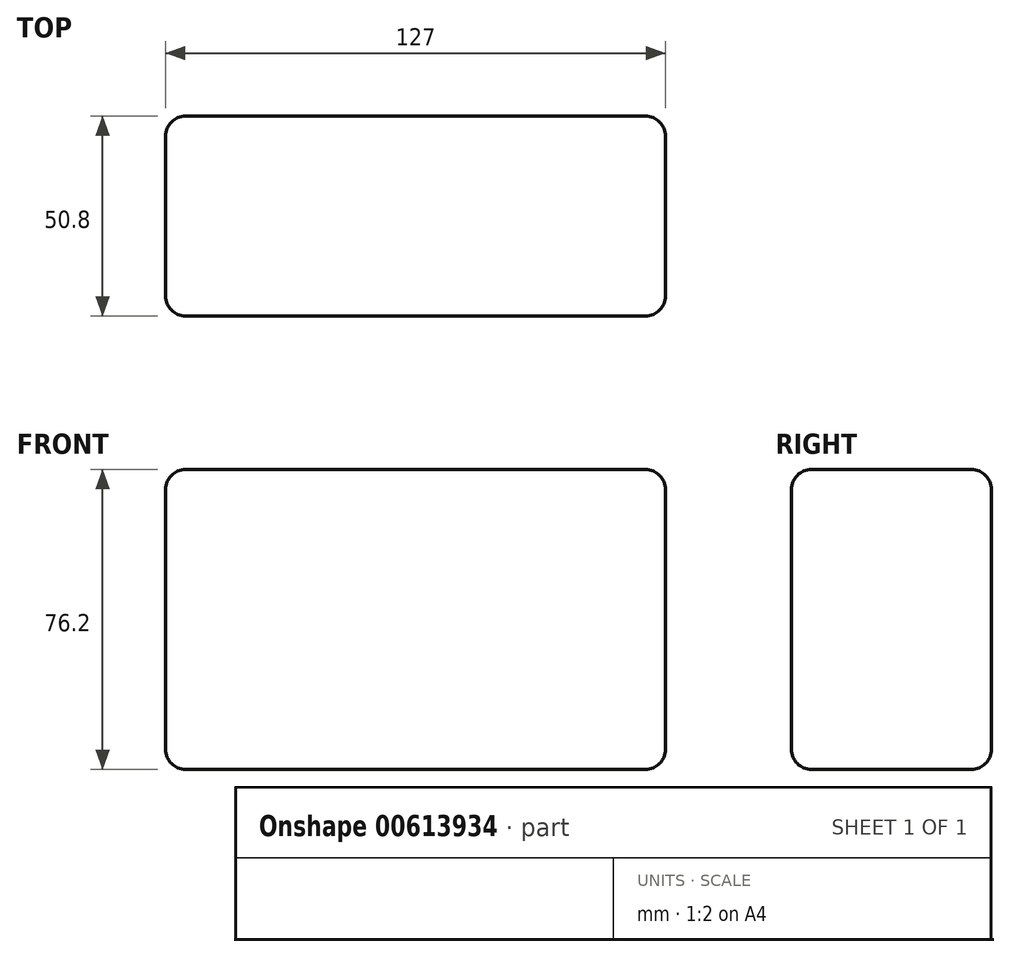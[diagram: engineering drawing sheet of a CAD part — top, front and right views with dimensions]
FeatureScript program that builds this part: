
annotation { "Feature Type Name" : "Feature", "Feature Type Description" : "" }
export const myFeature = defineFeature(function(context is Context, id is Id, definition is map)
    precondition{}
    {
        {
            var Q0;
            Q0=qCreatedBy(makeId("Top.planeOp"),FACE);
            var sketch = newSketch(context, id + "F0", { "sketchPlane" : qUnion([Q0])});
            skLineSegment(sketch, "E0.bottom", {"start": v(-50.5, 42.89) * mm, "end": v(76.5, 42.89) * mm});
            skLineSegment(sketch, "E0.top", {"start": v(-50.5, -7.91) * mm, "end": v(76.5, -7.91) * mm});
            skLineSegment(sketch, "E0.left", {"start": v(-50.5, 42.89) * mm, "end": v(-50.5, -7.91) * mm});
            skLineSegment(sketch, "E0.right", {"start": v(76.5, 42.89) * mm, "end": v(76.5, -7.91) * mm});
            skSolve(sketch);
        }
        {
            var Q0;
            Q0 = qSketchRegion(id + "F0", true);
            extrude(context, id + "F1", {"entities" : qUnion([Q0]), "depth" : 76.2 * mm, "offsetDistance" : 25.4 * mm});
        }
        {
            var Q0;
            Q0=makeQuery(id+"F1.opExtrude","CAP_EDGE",EDGE,{"disambiguationData":[OSD([sQuery(id+"F0.wireOp",EDGE,"E0.top")])],"isStart":false});
            var Q1;
            Q1=makeQuery(id+"F1.opExtrude","CAP_FACE",FACE,{"disambiguationData":[OSD([sQuery(id+"F0.wireOp",EDGE,"E0.bottom"),sQuery(id+"F0.wireOp",EDGE,"E0.top"),sQuery(id+"F0.wireOp",EDGE,"E0.left"),sQuery(id+"F0.wireOp",EDGE,"E0.right")])],"isStart":false});
            var Q2;
            Q2=makeQuery(id+"F1.opExtrude","SWEPT_FACE",FACE,{"disambiguationData":[OSD([sQuery(id+"F0.wireOp",EDGE,"E0.top")])]});
            var Q3;
            Q3=makeQuery(id+"F1.opExtrude","SWEPT_FACE",FACE,{"disambiguationData":[OSD([sQuery(id+"F0.wireOp",EDGE,"E0.right")])]});
            var Q4;
            Q4=makeQuery(id+"F1.opExtrude","SWEPT_FACE",FACE,{"disambiguationData":[OSD([sQuery(id+"F0.wireOp",EDGE,"E0.bottom")])]});
            var Q5;
            Q5=makeQuery(id+"F1.opExtrude","SWEPT_FACE",FACE,{"disambiguationData":[OSD([sQuery(id+"F0.wireOp",EDGE,"E0.left")])]});
            fillet(context, id + "F2", {"entities" : qUnion([Q0, Q1, Q2, Q3, Q4, Q5]), "radius" : 5.08 * mm, "tangentPropagation" : true, "allowEdgeOverflow" : false});
        }
    });
